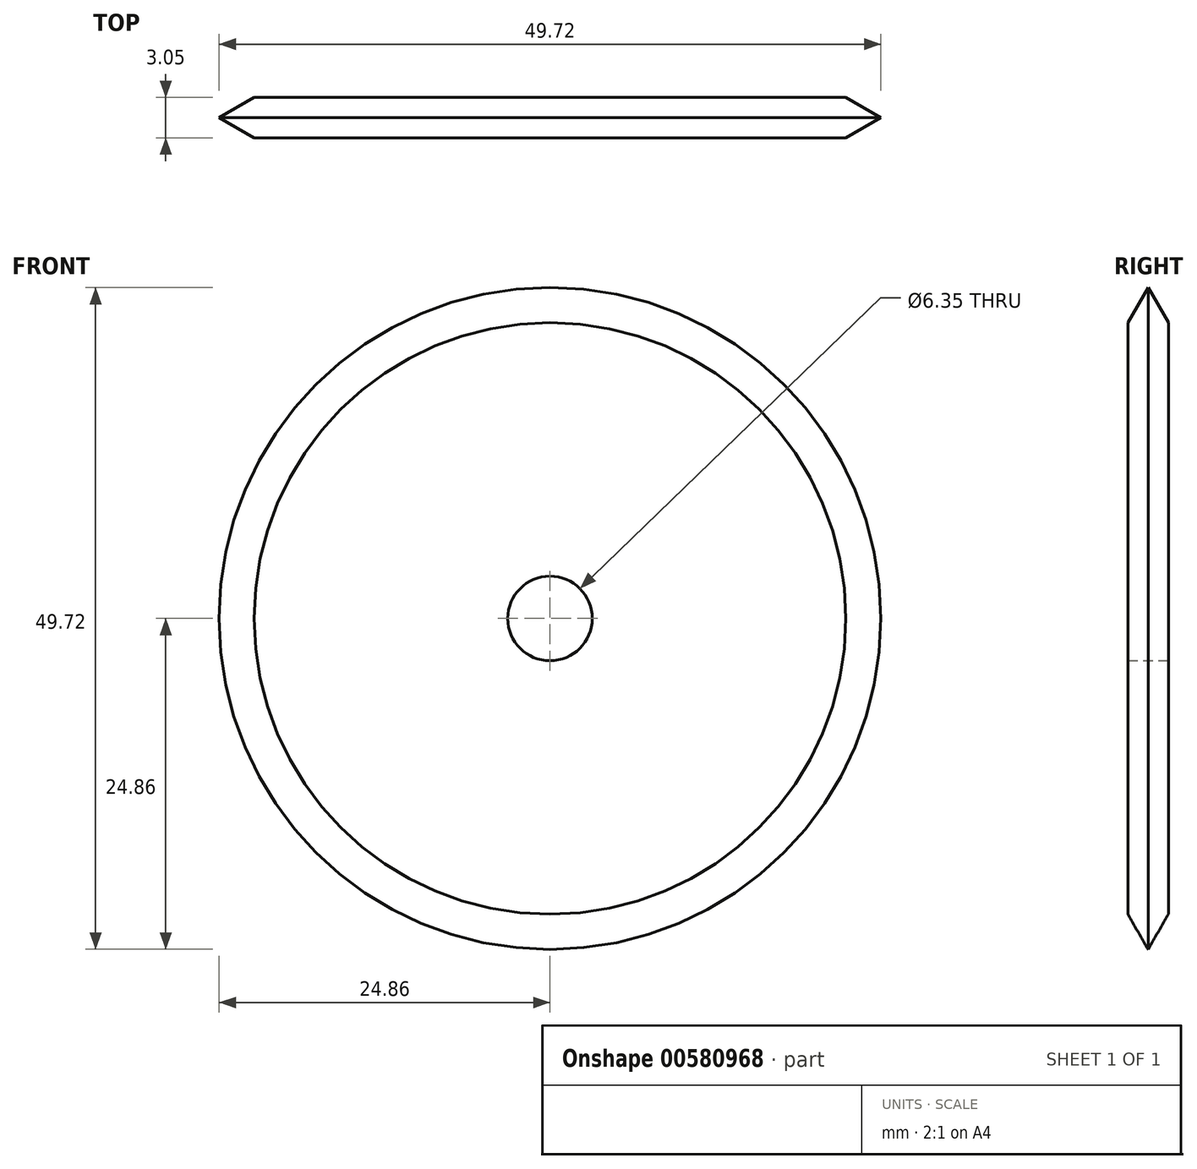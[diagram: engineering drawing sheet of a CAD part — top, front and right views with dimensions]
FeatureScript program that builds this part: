
annotation { "Feature Type Name" : "Feature", "Feature Type Description" : "" }
export const myFeature = defineFeature(function(context is Context, id is Id, definition is map)
    precondition{}
    {
        {
            var Q0;
            Q0=qCreatedBy(makeId("Front.planeOp"),FACE);
            var sketch = newSketch(context, id + "F0", { "sketchPlane" : qUnion([Q0])});
            skCircle(sketch, "E0", {"center": v(0, 0) * mm, "radius": 25.4 * mm});
            skCircle(sketch, "E1", {"center": v(0, 0) * mm, "radius": 3.18 * mm});
            skSolve(sketch);
        }
        {
            var Q0;
            Q0=makeQuery(id+"F0.imprint","IMPRINT",FACE,{"disambiguationData":[TD([[makeQuery(id+"F0.imprint","IMPRINT",EDGE,{"derivedFrom":sQuery(id+"F0.wireOp",EDGE,"E0")}),1.0]])]});
            extrude(context, id + "F1", {"entities" : qUnion([Q0]), "depth" : 3.05 * mm, "offsetDistance" : 25.4 * mm});
        }
        {
            var Q0;
            Q0=makeQuery(id+"F1.opExtrude","CAP_EDGE",EDGE,{"disambiguationData":[OSD([sQuery(id+"F0.wireOp",EDGE,"E0")])],"isStart":false});
            chamfer(context, id + "F2", {"entities" : qUnion([Q0]), "chamferType" : ChamferType.OFFSET_ANGLE, "width" : 3.17 * mm, "oppositeDirection" : false, "angle" : 30 * degree, "tangentPropagation" : true});
        }
        {
            var Q0;
            Q0=makeQuery(id+"F1.opExtrude","CAP_EDGE",EDGE,{"disambiguationData":[OSD([sQuery(id+"F0.wireOp",EDGE,"E0")])],"isStart":true});
            chamfer(context, id + "F3", {"entities" : qUnion([Q0]), "chamferType" : ChamferType.OFFSET_ANGLE, "width" : 3.17 * mm, "oppositeDirection" : true, "angle" : 30 * degree, "tangentPropagation" : true});
        }
    });
